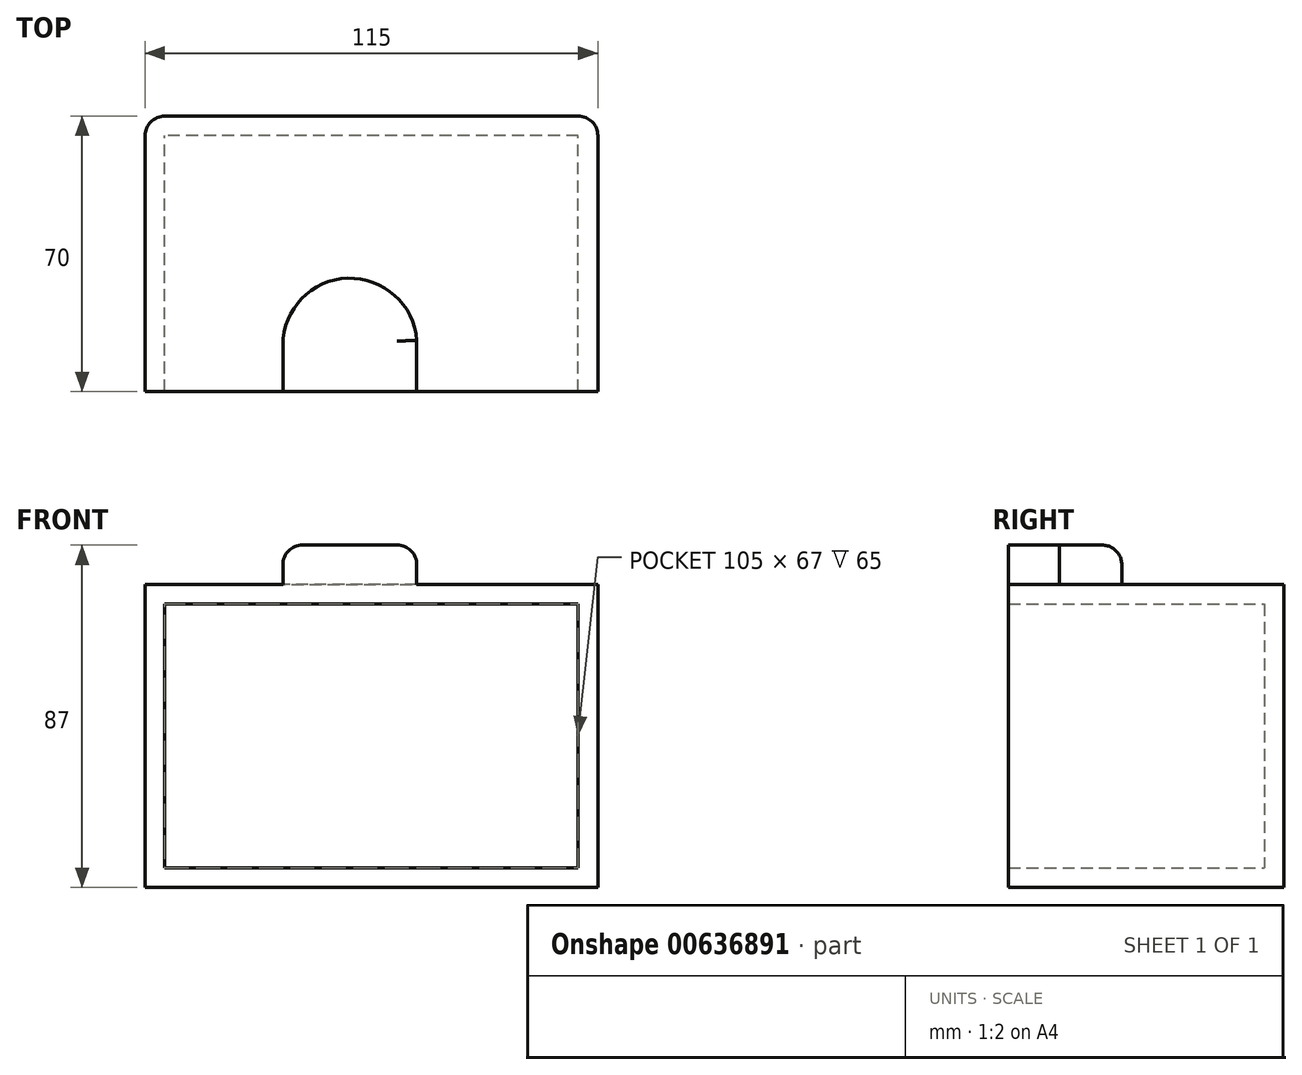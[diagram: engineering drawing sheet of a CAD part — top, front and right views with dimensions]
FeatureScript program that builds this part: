
annotation { "Feature Type Name" : "Feature", "Feature Type Description" : "" }
export const myFeature = defineFeature(function(context is Context, id is Id, definition is map)
    precondition{}
    {
        {
            var Q0;
            Q0=qCreatedBy(makeId("Front.planeOp"),FACE);
            var sketch = newSketch(context, id + "F0", { "sketchPlane" : qUnion([Q0])});
            skLineSegment(sketch, "E0.bottom", {"start": v(-64.44, 59.7) * mm, "end": v(50.56, 59.7) * mm});
            skLineSegment(sketch, "E0.top", {"start": v(-64.44, -17.3) * mm, "end": v(50.56, -17.3) * mm});
            skLineSegment(sketch, "E0.left", {"start": v(-64.44, 59.7) * mm, "end": v(-64.44, -17.3) * mm});
            skLineSegment(sketch, "E0.right", {"start": v(50.56, 59.7) * mm, "end": v(50.56, -17.3) * mm});
            skLineSegment(sketch, "E1.bottom", {"start": v(45.56, 54.7) * mm, "end": v(-59.44, 54.7) * mm});
            skLineSegment(sketch, "E1.top", {"start": v(45.56, -12.3) * mm, "end": v(-59.44, -12.3) * mm});
            skLineSegment(sketch, "E1.left", {"start": v(45.56, 54.7) * mm, "end": v(45.56, -12.3) * mm});
            skLineSegment(sketch, "E1.right", {"start": v(-59.44, 54.7) * mm, "end": v(-59.44, -12.3) * mm});
            skSolve(sketch);
        }
        {
            var Q0;
            Q0 = qSketchRegion(id + "F0", true);
            extrude(context, id + "F1", {"entities" : qUnion([Q0]), "depth" : 70 * mm, "offsetDistance" : 25 * mm});
        }
        {
            var Q0;
            Q0=qCreatedBy(makeId("Front.planeOp"),FACE);
            var sketch = newSketch(context, id + "F2", { "sketchPlane" : qUnion([Q0])});
            skLineSegment(sketch, "E2.bottom", {"start": v(-60.79, 55.81) * mm, "end": v(46.75, 55.81) * mm});
            skLineSegment(sketch, "E2.top", {"start": v(-60.79, -13.38) * mm, "end": v(46.75, -13.38) * mm});
            skLineSegment(sketch, "E2.left", {"start": v(-60.79, 55.81) * mm, "end": v(-60.79, -13.38) * mm});
            skLineSegment(sketch, "E2.right", {"start": v(46.75, 55.81) * mm, "end": v(46.75, -13.38) * mm});
            skSolve(sketch);
        }
        {
            var Q0;
            Q0 = qSketchRegion(id + "F2", true);
            extrude(context, id + "F3", {"entities" : qUnion([Q0]), "operationType" : NewBodyOperationType.ADD, "depth" : 5 * mm, "offsetDistance" : 25 * mm});
        }
        {
            var Q0;
            Q0=makeQuery(id+"F1.opExtrude","SWEPT_FACE",FACE,{"disambiguationData":[OSD([sQuery(id+"F0.wireOp",EDGE,"E0.bottom")])]});
            var sketch = newSketch(context, id + "F4", { "sketchPlane" : qUnion([Q0])});
            skPoint(sketch, "E3.endSnap0", {"position": v(15.98, -49.42) * mm});
            skArc(sketch, "E4", {"start": v(4.56, -57) * mm, "mid": v(-13.03, -41.2) * mm, "end": v(-29.44, -58.22) * mm});
            skLineSegment(sketch, "E5", {"start": v(4.56, -70) * mm, "end": v(4.56, -57) * mm});
            skLineSegment(sketch, "E6", {"start": v(-29.44, -58.22) * mm, "end": v(-29.44, -70) * mm});
            skLineSegment(sketch, "E7", {"start": v(-29.44, -70) * mm, "end": v(4.56, -70) * mm});
            skSolve(sketch);
        }
        {
            var Q0;
            Q0 = qSketchRegion(id + "F4", true);
            extrude(context, id + "F5", {"entities" : qUnion([Q0]), "operationType" : NewBodyOperationType.ADD, "depth" : 10 * mm, "offsetDistance" : 25 * mm});
        }
        {
            var Q0;
            Q0=makeQuery(id+"F1.opExtrude","CAP_EDGE",EDGE,{"disambiguationData":[OSD([sQuery(id+"F0.wireOp",EDGE,"E0.left")])],"isStart":true});
            var Q1;
            Q1=makeQuery(id+"F1.opExtrude","CAP_EDGE",EDGE,{"disambiguationData":[OSD([sQuery(id+"F0.wireOp",EDGE,"E0.right")])],"isStart":true});
            fillet(context, id + "F6", {"entities" : qUnion([Q0, Q1]), "radius" : 5 * mm, "tangentPropagation" : true, "allowEdgeOverflow" : false});
        }
        {
            var Q0;
            Q0=makeQuery(id+"F5.opExtrude","CAP_EDGE",EDGE,{"disambiguationData":[OSD([sQuery(id+"F4.wireOp",EDGE,"E6")])],"isStart":false});
            var Q1;
            Q1=makeQuery(id+"F5.opExtrude","CAP_EDGE",EDGE,{"disambiguationData":[OSD([sQuery(id+"F4.wireOp",EDGE,"E5")])],"isStart":false});
            fillet(context, id + "F7", {"entities" : qUnion([Q0, Q1]), "radius" : 5 * mm, "tangentPropagation" : true, "allowEdgeOverflow" : false});
        }
    });
